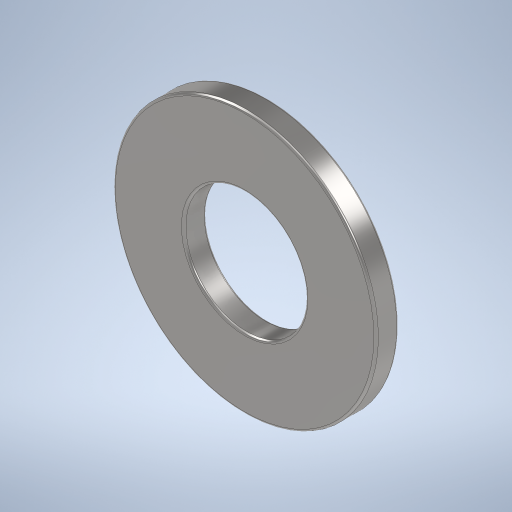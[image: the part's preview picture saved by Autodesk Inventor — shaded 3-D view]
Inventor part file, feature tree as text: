
AUTODESK INVENTOR PART (.ipt)
format: ipt  version: 2024 (Build 280153000, 153)  size: 263,680 bytes
history: native  units: in
note: dims shown in document units (in); Inventor stores cm internally (conversion verified against a paired STEP export)
features: fillet x1
ambient origin geometry x8: Origin, YZ Plane, XZ Plane, XY Plane, X Axis, Y Axis, Z Axis, Center Point
bodies: Solid1 (feature_tree)
feature tree (1):
  fillet  "Fillet1"  [1 undecoded]
note: 1 required parameter value undecoded (feature->parameter linkage not recoverable at this tier; creation-order binding heuristic only, values carry confidence <= 0.55)
